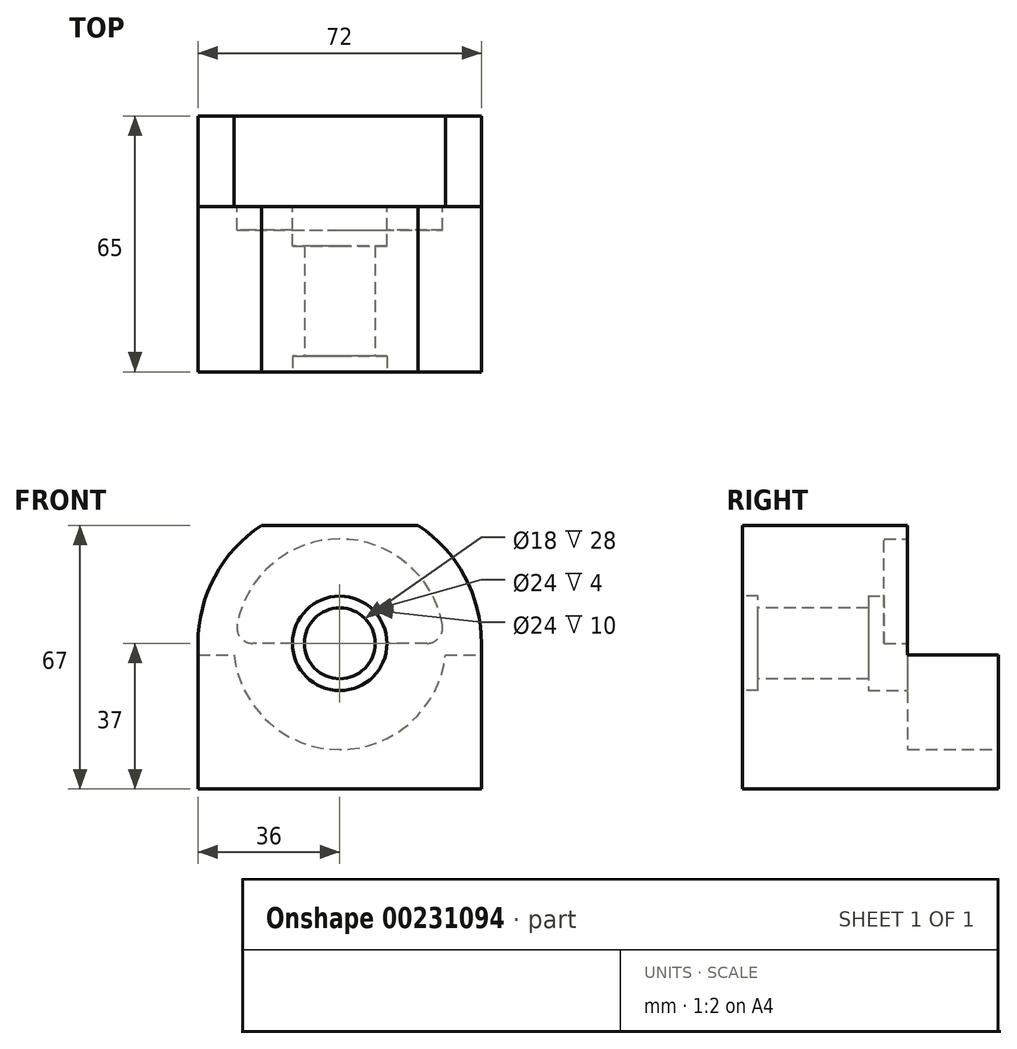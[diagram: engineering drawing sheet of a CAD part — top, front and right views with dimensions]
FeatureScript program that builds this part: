
annotation { "Feature Type Name" : "Feature", "Feature Type Description" : "" }
export const myFeature = defineFeature(function(context is Context, id is Id, definition is map)
    precondition{}
    {
        {
            var Q0;
            Q0=qCreatedBy(makeId("Front.planeOp"),FACE);
            var sketch = newSketch(context, id + "F0", { "sketchPlane" : qUnion([Q0])});
            skArc(sketch, "E0", {"start": v(36, 0) * mm, "mid": v(0, 36) * mm, "end": v(-36, 0) * mm});
            skLineSegment(sketch, "E1.top", {"start": v(-36, -37) * mm, "end": v(36, -37) * mm});
            skLineSegment(sketch, "E1.left", {"start": v(-36, 0) * mm, "end": v(-36, -37) * mm});
            skLineSegment(sketch, "E1.right", {"start": v(36, 0) * mm, "end": v(36, -37) * mm});
            skCircle(sketch, "E2", {"center": v(0, 0) * mm, "radius": 9 * mm});
            skSolve(sketch);
        }
        {
            var Q0;
            Q0 = qSketchRegion(id + "F0", true);
            extrude(context, id + "F1", {"entities" : qUnion([Q0]), "oppositeDirection" : true, "depth" : 65 * mm});
        }
        {
            var Q0;
            Q0=makeQuery(id+"F1.opExtrude","SWEPT_FACE",FACE,{"disambiguationData":[OSD([sQuery(id+"F0.wireOp",EDGE,"E1.right")])]});
            var sketch = newSketch(context, id + "F2", { "sketchPlane" : qUnion([Q0])});
            skLineSegment(sketch, "E3.bottom", {"start": v(42, 36) * mm, "end": v(65, 36) * mm});
            skLineSegment(sketch, "E3.top", {"start": v(42, -3) * mm, "end": v(65, -3) * mm});
            skLineSegment(sketch, "E3.left", {"start": v(42, 36) * mm, "end": v(42, -3) * mm});
            skLineSegment(sketch, "E3.right", {"start": v(65, 36) * mm, "end": v(65, -3) * mm});
            skLineSegment(sketch, "E4.0.1", {"start": v(0, 0) * mm, "end": v(65, 0) * mm});
            skLineSegment(sketch, "E4.0.2", {"start": v(65, 0) * mm, "end": v(65, 36) * mm});
            skLineSegment(sketch, "E4.0.3", {"start": v(65, 0) * mm, "end": v(0, 0) * mm});
            skSolve(sketch);
        }
        {
            var Q0;
            {var subQ0=sQuery(id+"F2.wireOp",EDGE,"E3.bottom");Q0=makeQuery(id+"F2.imprint","IMPRINT",FACE,{"disambiguationData":[TD([[makeQuery(id+"F2.imprint","IMPRINT",EDGE,{"derivedFrom":subQ0}),-1.0]])]});}
            var Q1;
            {var subQ0=sQuery(id+"F2.wireOp",EDGE,"E3.top");Q1=makeQuery(id+"F2.imprint","IMPRINT",FACE,{"disambiguationData":[TD([[makeQuery(id+"F2.imprint","IMPRINT",EDGE,{"derivedFrom":subQ0}),1.0]])]});}
            extrude(context, id + "F3", {"entities" : qUnion([Q0, Q1]), "operationType" : NewBodyOperationType.REMOVE, "oppositeDirection" : true, "depth" : 72 * mm});
        }
        {
            var Q0;
            Q0=makeQuery(id+"F1.opExtrude","CAP_FACE",FACE,{"disambiguationData":[OSD([sQuery(id+"F0.wireOp",EDGE,"E0"),sQuery(id+"F0.wireOp",EDGE,"E1.top"),sQuery(id+"F0.wireOp",EDGE,"E1.left"),sQuery(id+"F0.wireOp",EDGE,"E1.right"),sQuery(id+"F0.wireOp",EDGE,"E2")])],"isStart":true});
            var sketch = newSketch(context, id + "F4", { "sketchPlane" : qUnion([Q0])});
            skCircle(sketch, "E5", {"center": v(0, 0) * mm, "radius": 12 * mm});
            skSolve(sketch);
        }
        {
            var Q0;
            Q0 = qSketchRegion(id + "F4", true);
            extrude(context, id + "F5", {"entities" : qUnion([Q0]), "operationType" : NewBodyOperationType.REMOVE, "oppositeDirection" : true, "depth" : 4 * mm});
        }
        {
            var Q0;
            Q0=makeQuery(id+"F1.opExtrude","CAP_FACE",FACE,{"disambiguationData":[OSD([sQuery(id+"F0.wireOp",EDGE,"E0"),sQuery(id+"F0.wireOp",EDGE,"E1.top"),sQuery(id+"F0.wireOp",EDGE,"E1.left"),sQuery(id+"F0.wireOp",EDGE,"E1.right"),sQuery(id+"F0.wireOp",EDGE,"E2")])],"isStart":false});
            var sketch = newSketch(context, id + "F6", { "sketchPlane" : qUnion([Q0])});
            skCircle(sketch, "E6", {"center": v(0, 0) * mm, "radius": 27 * mm});
            skSolve(sketch);
        }
        {
            var Q0;
            Q0 = qSketchRegion(id + "F6", true);
            extrude(context, id + "F7", {"entities" : qUnion([Q0]), "operationType" : NewBodyOperationType.REMOVE, "oppositeDirection" : true, "depth" : 23 * mm});
        }
        {
            var Q0;
            Q0=makeQuery(id+"F7.boolean.opBoolean","MERGE",FACE,{"derivedFrom":[makeQuery(id+"F3.boolean.opBoolean","COPY",FACE,{"derivedFrom":makeQuery(id+"F3.opExtrude","SWEPT_FACE",FACE,{"disambiguationData":[OSD([sQuery(id+"F2.wireOp",EDGE,"E3.left")])]})}),makeQuery(id+"F7.opExtrude","CAP_FACE",FACE,{"disambiguationData":[OSD([sQuery(id+"F6.wireOp",EDGE,"E6")])],"isStart":false})]});
            var sketch = newSketch(context, id + "F8", { "sketchPlane" : qUnion([Q0])});
            skCircle(sketch, "E7", {"center": v(0, 0) * mm, "radius": 12 * mm});
            skSolve(sketch);
        }
        {
            var Q0;
            Q0 = qSketchRegion(id + "F8", true);
            extrude(context, id + "F9", {"entities" : qUnion([Q0]), "operationType" : NewBodyOperationType.REMOVE, "oppositeDirection" : true, "depth" : 10 * mm});
        }
        {
            var Q0;
            Q0=makeQuery(id+"F7.boolean.opBoolean","MERGE",FACE,{"derivedFrom":[makeQuery(id+"F3.boolean.opBoolean","COPY",FACE,{"derivedFrom":makeQuery(id+"F3.opExtrude","SWEPT_FACE",FACE,{"disambiguationData":[OSD([sQuery(id+"F2.wireOp",EDGE,"E3.left")])]})}),makeQuery(id+"F7.opExtrude","CAP_FACE",FACE,{"disambiguationData":[OSD([sQuery(id+"F6.wireOp",EDGE,"E6")])],"isStart":false})]});
            var sketch = newSketch(context, id + "F10", { "sketchPlane" : qUnion([Q0])});
            skArc(sketch, "E8", {"start": v(26.08, 4.71) * mm, "mid": v(0, 26.5) * mm, "end": v(-26.08, 4.71) * mm});
            skLineSegment(sketch, "E9", {"start": v(-22.14, 0) * mm, "end": v(22.14, 0) * mm});
            skPoint(sketch, "E10.visualSharp", {"position": v(-26.5, 0) * mm});
            skArc(sketch, "E10.filletArc", {"start": v(-26.08, 4.71) * mm, "mid": v(-25.21, 1.44) * mm, "end": v(-22.14, 0) * mm});
            skPoint(sketch, "E11.visualSharp", {"position": v(26.5, 0) * mm});
            skArc(sketch, "E11.filletArc", {"start": v(22.14, 0) * mm, "mid": v(25.21, 1.44) * mm, "end": v(26.08, 4.71) * mm});
            skSolve(sketch);
        }
        {
            var Q0;
            Q0 = qSketchRegion(id + "F10", true);
            extrude(context, id + "F11", {"entities" : qUnion([Q0]), "operationType" : NewBodyOperationType.REMOVE, "oppositeDirection" : true, "depth" : 6 * mm});
        }
        {
            var Q0;
            Q0=makeQuery(id+"F1.opExtrude","CAP_FACE",FACE,{"disambiguationData":[OSD([sQuery(id+"F0.wireOp",EDGE,"E0"),sQuery(id+"F0.wireOp",EDGE,"E1.top"),sQuery(id+"F0.wireOp",EDGE,"E1.left"),sQuery(id+"F0.wireOp",EDGE,"E1.right"),sQuery(id+"F0.wireOp",EDGE,"E2")])],"isStart":true});
            var sketch = newSketch(context, id + "F12", { "sketchPlane" : qUnion([Q0])});
            skLineSegment(sketch, "E12", {"start": v(-19.9, 30) * mm, "end": v(19.9, 30) * mm});
            skSolve(sketch);
        }
        {
            var Q0;
            {var subQ0=sQuery(id+"F12.wireOp",EDGE,"E12");Q0=makeQuery(id+"F12.imprint","IMPRINT",FACE,{"disambiguationData":[TD([[makeQuery(id+"F12.imprint","IMPRINT",EDGE,{"derivedFrom":subQ0}),1.0]])]});}
            extrude(context, id + "F13", {"entities" : qUnion([Q0]), "operationType" : NewBodyOperationType.REMOVE, "oppositeDirection" : true, "depth" : 65 * mm});
        }
    });
